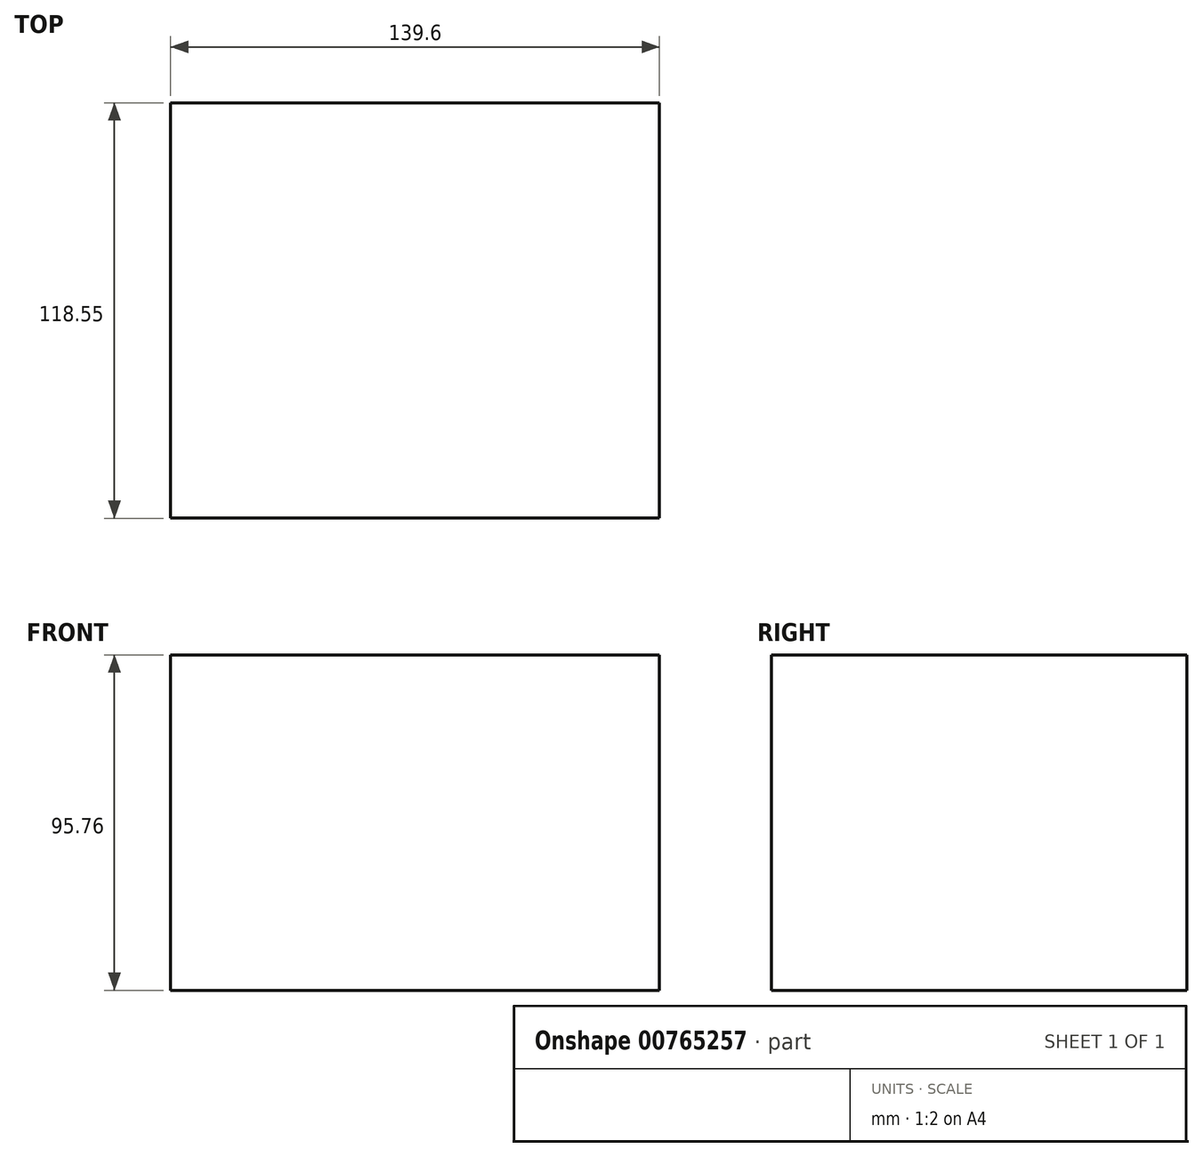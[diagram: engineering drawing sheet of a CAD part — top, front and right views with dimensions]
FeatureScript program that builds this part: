
annotation { "Feature Type Name" : "Feature", "Feature Type Description" : "" }
export const myFeature = defineFeature(function(context is Context, id is Id, definition is map)
    precondition{}
    {
        {
            var Q0;
            Q0=qCreatedBy(makeId("Top.planeOp"),FACE);
            var sketch = newSketch(context, id + "F0", { "sketchPlane" : qUnion([Q0])});
            skLineSegment(sketch, "E0.bottom", {"start": v(-76.62, -74.96) * mm, "end": v(75.17, -74.96) * mm});
            skLineSegment(sketch, "E0.top", {"start": v(-76.62, 55.77) * mm, "end": v(75.17, 55.77) * mm});
            skLineSegment(sketch, "E0.left", {"start": v(-76.62, -74.96) * mm, "end": v(-76.62, 55.77) * mm});
            skLineSegment(sketch, "E0.right", {"start": v(75.17, -74.96) * mm, "end": v(75.17, 55.77) * mm});
            skLineSegment(sketch, "E1.0", {"start": v(69.07, -68.87) * mm, "end": v(69.07, 49.68) * mm});
            skLineSegment(sketch, "E1.1", {"start": v(-70.53, -68.87) * mm, "end": v(69.07, -68.87) * mm});
            skLineSegment(sketch, "E1.2", {"start": v(-70.53, -68.87) * mm, "end": v(-70.53, 49.68) * mm});
            skLineSegment(sketch, "E1.3", {"start": v(-70.53, 49.68) * mm, "end": v(69.07, 49.68) * mm});
            skSolve(sketch);
        }
        {
            var Q0;
            Q0=makeQuery(id+"F0.imprint","IMPRINT",FACE,{"disambiguationData":[TD([[makeQuery(id+"F0.imprint","IMPRINT",EDGE,{"derivedFrom":sQuery(id+"F0.wireOp",EDGE,"E1.0")}),1.0]])]});
            extrude(context, id + "F1", {"entities" : qUnion([Q0]), "depth" : 95.76 * mm, "offsetDistance" : 25.4 * mm});
        }
    });
